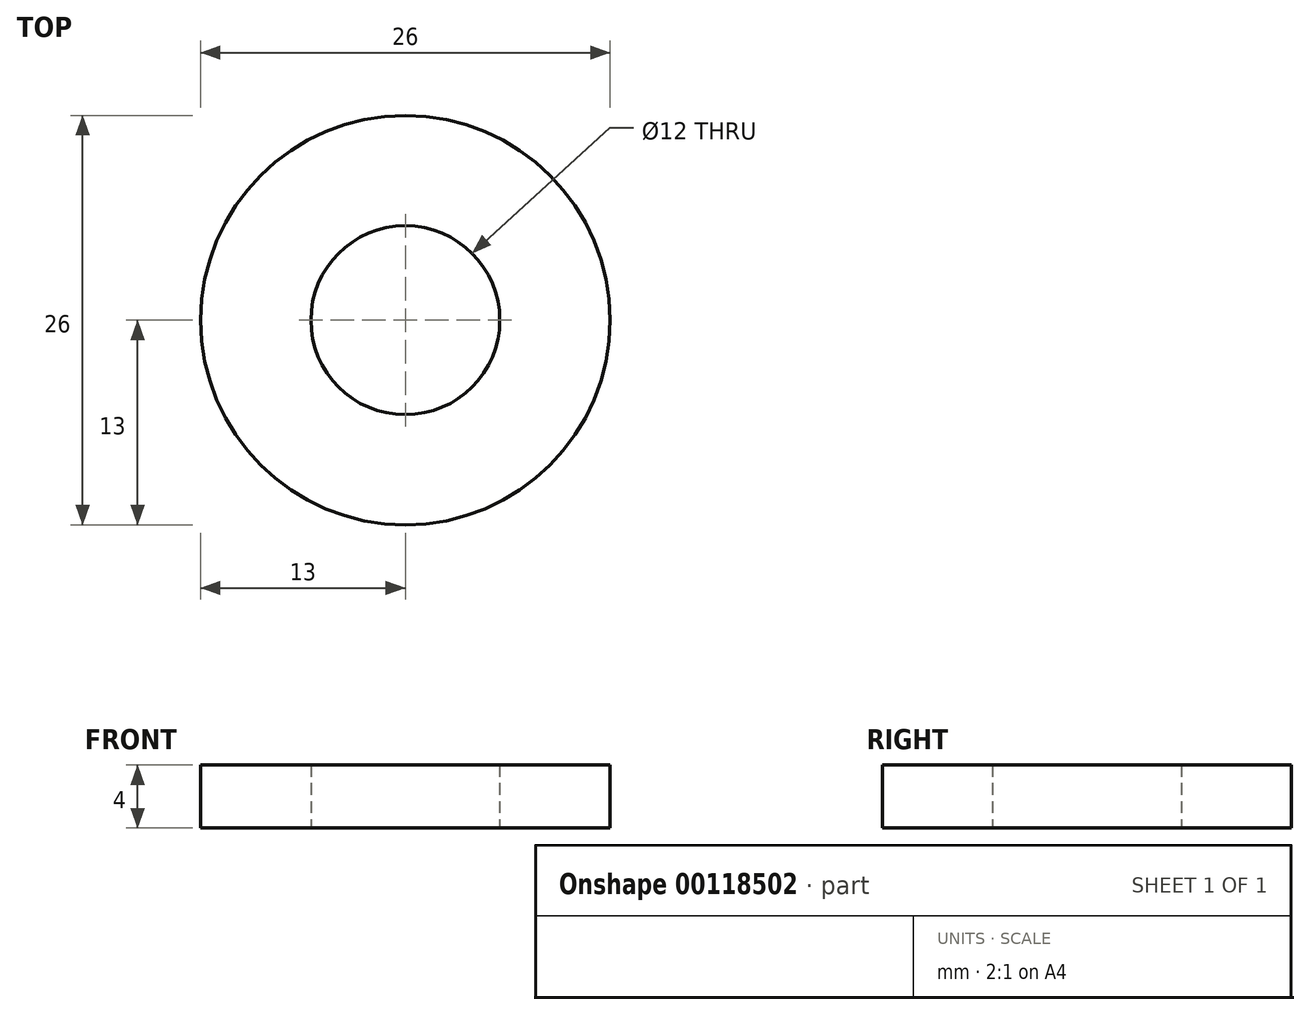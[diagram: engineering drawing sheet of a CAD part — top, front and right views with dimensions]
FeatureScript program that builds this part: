
annotation { "Feature Type Name" : "Feature", "Feature Type Description" : "" }
export const myFeature = defineFeature(function(context is Context, id is Id, definition is map)
    precondition{}
    {
        {
            var Q0;
            Q0=qCreatedBy(makeId("Top.planeOp"),FACE);
            var sketch = newSketch(context, id + "F0", { "sketchPlane" : qUnion([Q0])});
            skCircle(sketch, "E0", {"center": v(0, 0) * mm, "radius": 6 * mm});
            skCircle(sketch, "E1", {"center": v(0, 0) * mm, "radius": 13 * mm});
            skSolve(sketch);
        }
        {
            var Q0;
            Q0 = qSketchRegion(id + "F0", true);
            extrude(context, id + "F1", {"entities" : qUnion([Q0]), "depth" : 4 * mm});
        }
    });
